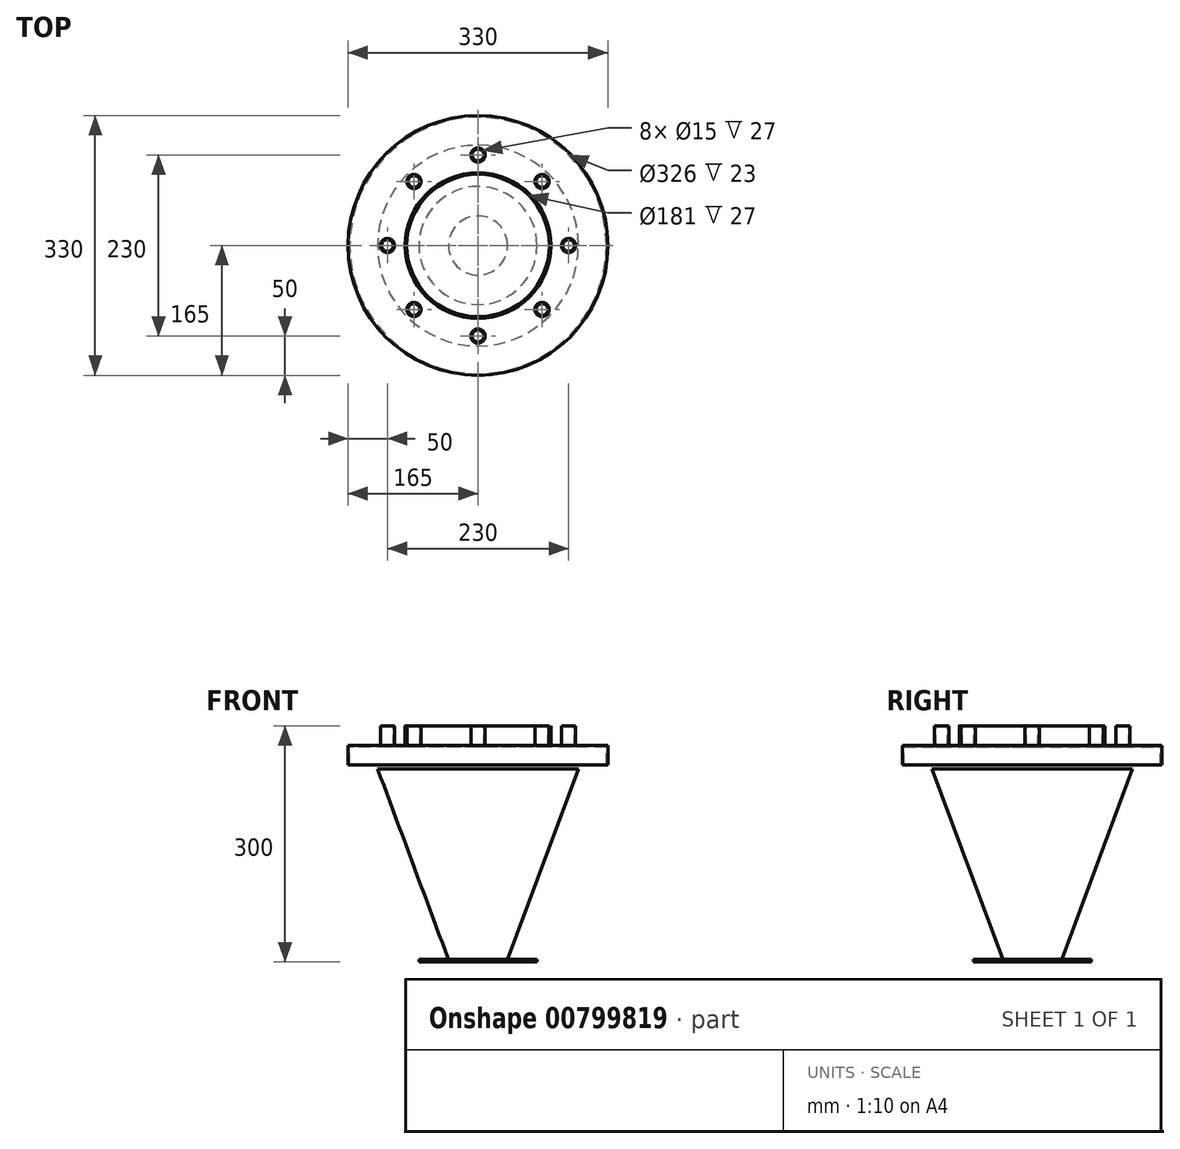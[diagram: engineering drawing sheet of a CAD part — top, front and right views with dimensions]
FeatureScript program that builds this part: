
annotation { "Feature Type Name" : "Feature", "Feature Type Description" : "" }
export const myFeature = defineFeature(function(context is Context, id is Id, definition is map)
    precondition{}
    {
        {
            var Q0;
            Q0=qCreatedBy(makeId("Front.planeOp"),FACE);
            var sketch = newSketch(context, id + "F0", { "sketchPlane" : qUnion([Q0])});
            skLineSegment(sketch, "E0", {"start": v(0, 0) * mm, "end": v(-127.5, 0) * mm});
            skLineSegment(sketch, "E1", {"start": v(-127.5, 0) * mm, "end": v(-37.5, -242) * mm});
            skLineSegment(sketch, "E2", {"start": v(-37.5, -242) * mm, "end": v(-75, -242) * mm});
            skLineSegment(sketch, "E3", {"start": v(-75, -242) * mm, "end": v(-75, -245) * mm});
            skLineSegment(sketch, "E4", {"start": v(-75, -245) * mm, "end": v(0, -245) * mm});
            skLineSegment(sketch, "E5", {"start": v(0, -245) * mm, "end": v(0, 0) * mm});
            skSolve(sketch);
        }
        {
            var Q0;
            Q0=makeQuery(id+"F0.imprint","IMPRINT",FACE,{"disambiguationData":[TD([[makeQuery(id+"F0.imprint","IMPRINT",EDGE,{"derivedFrom":sQuery(id+"F0.wireOp",EDGE,"E0")}),1.0]])]});
            var Q1;
            Q1=sQuery(id+"F0.wireOp",EDGE,"E5");
            revolve(context, id + "F1", {"surfaceOperationType" : NewSurfaceOperationType.NEW, "entities" : qUnion([Q0]), "axis" : qUnion([Q1]), "revolveType" : RevolveType.FULL});
        }
        {
            var Q0;
            Q0=qCreatedBy(makeId("Top.planeOp"),FACE);
            cPlane(context, id + "F2", {"entities" : qUnion([Q0]), "cplaneType" : CPlaneType.OFFSET, "offset" : 30 * mm, "width" : 150 * mm, "height" : 150 * mm});
        }
        {
            var Q0;
            Q0=qCreatedBy(id+"F2.planeOp",FACE);
            var sketch = newSketch(context, id + "F3", { "sketchPlane" : qUnion([Q0])});
            skCircle(sketch, "E6", {"center": v(0, 0) * mm, "radius": 165 * mm});
            skSolve(sketch);
        }
        {
            var Q0;
            Q0=makeQuery(id+"F3.imprint","IMPRINT",FACE,{"disambiguationData":[TD([[makeQuery(id+"F3.imprint","IMPRINT",EDGE,{"derivedFrom":sQuery(id+"F3.wireOp",EDGE,"E6")}),1.0]])]});
            extrude(context, id + "F4", {"entities" : qUnion([Q0]), "oppositeDirection" : true, "depth" : 25 * mm, "offsetDistance" : 25 * mm});
        }
        {
            var Q0;
            Q0=makeQuery(id+"F4.opExtrude","CAP_FACE",FACE,{"disambiguationData":[OSD([sQuery(id+"F3.wireOp",EDGE,"E6")])],"isStart":false});
            shell(context, id + "F5", {"entities" : qUnion([Q0]), "thickness" : 2 * mm});
        }
        {
            var Q0;
            Q0=qCreatedBy(id+"F2.planeOp",FACE);
            var sketch = newSketch(context, id + "F6", { "sketchPlane" : qUnion([Q0])});
            skCircle(sketch, "E7", {"center": v(0, 0) * mm, "radius": 92.5 * mm});
            skSolve(sketch);
        }
        {
            var Q0;
            Q0 = qSketchRegion(id + "F6", true);
            extrude(context, id + "F7", {"entities" : qUnion([Q0]), "operationType" : NewBodyOperationType.ADD, "depth" : 25 * mm, "offsetDistance" : 25 * mm});
        }
        {
            var Q0;
            Q0=makeQuery(id+"F7.opExtrude","CAP_FACE",FACE,{"disambiguationData":[OSD([sQuery(id+"F6.wireOp",EDGE,"E7")])],"isStart":false});
            shell(context, id + "F8", {"entities" : qUnion([Q0]), "thickness" : 2 * mm});
        }
        {
            var Q0;
            Q0=makeQuery(id+"F4.opExtrude","CAP_FACE",FACE,{"disambiguationData":[OSD([sQuery(id+"F3.wireOp",EDGE,"E6")])],"isStart":true});
            var sketch = newSketch(context, id + "F9", { "sketchPlane" : qUnion([Q0])});
            skCircle(sketch, "E8", {"center": v(0, 0) * mm, "radius": 90.5 * mm});
            skSolve(sketch);
        }
        {
            var Q0;
            Q0 = qSketchRegion(id + "F9", true);
            extrude(context, id + "F10", {"entities" : qUnion([Q0]), "operationType" : NewBodyOperationType.REMOVE, "oppositeDirection" : true, "depth" : 17 * mm, "offsetDistance" : 25 * mm});
        }
        {
            var Q0;
            Q0=makeQuery(id+"F4.opExtrude","CAP_FACE",FACE,{"disambiguationData":[OSD([sQuery(id+"F3.wireOp",EDGE,"E6")])],"isStart":true});
            var sketch = newSketch(context, id + "F11", { "sketchPlane" : qUnion([Q0])});
            skCircle(sketch, "E9", {"center": v(0, 115) * mm, "radius": 7.5 * mm});
            skCircle(sketch, "E10.1.0", {"center": v(-81.32, 81.32) * mm, "radius": 7.5 * mm});
            skCircle(sketch, "E10.2.0", {"center": v(-115, 0) * mm, "radius": 7.5 * mm});
            skCircle(sketch, "E10.3.0", {"center": v(-81.32, -81.32) * mm, "radius": 7.5 * mm});
            skCircle(sketch, "E10.4.0", {"center": v(0, -115) * mm, "radius": 7.5 * mm});
            skCircle(sketch, "E10.5.0", {"center": v(81.32, -81.32) * mm, "radius": 7.5 * mm});
            skCircle(sketch, "E10.6.0", {"center": v(115, 0) * mm, "radius": 7.5 * mm});
            skCircle(sketch, "E10.7.0", {"center": v(81.32, 81.32) * mm, "radius": 7.5 * mm});
            skPoint(sketch, "E10.center", {"position": v(0, 0) * mm});
            skSolve(sketch);
        }
        {
            var Q0;
            Q0 = qSketchRegion(id + "F11", true);
            extrude(context, id + "F12", {"entities" : qUnion([Q0]), "operationType" : NewBodyOperationType.REMOVE, "oppositeDirection" : true, "depth" : 25 * mm, "offsetDistance" : 25 * mm});
        }
        {
            var Q0;
            Q0=makeQuery(id+"F4.opExtrude","CAP_FACE",FACE,{"disambiguationData":[OSD([sQuery(id+"F3.wireOp",EDGE,"E6")])],"isStart":true});
            var sketch = newSketch(context, id + "F13", { "sketchPlane" : qUnion([Q0])});
            skCircle(sketch, "E11", {"center": v(0, 115) * mm, "radius": 7.5 * mm});
            skCircle(sketch, "E12", {"center": v(0, 115) * mm, "radius": 9 * mm});
            skCircle(sketch, "E13.3.0", {"center": v(0, -115) * mm, "radius": 9 * mm});
            skPoint(sketch, "E13.center", {"position": v(0, 0) * mm});
            skCircle(sketch, "E14.1.0", {"center": v(-81.32, 81.32) * mm, "radius": 7.5 * mm});
            skCircle(sketch, "E14.1.1", {"center": v(-81.32, 81.32) * mm, "radius": 9 * mm});
            skCircle(sketch, "E14.2.0", {"center": v(-115, 0) * mm, "radius": 7.5 * mm});
            skCircle(sketch, "E14.2.1", {"center": v(-115, 0) * mm, "radius": 9 * mm});
            skCircle(sketch, "E14.3.0", {"center": v(-81.32, -81.32) * mm, "radius": 7.5 * mm});
            skCircle(sketch, "E14.3.1", {"center": v(-81.32, -81.32) * mm, "radius": 9 * mm});
            skCircle(sketch, "E14.4.0", {"center": v(0, -115) * mm, "radius": 7.5 * mm});
            skCircle(sketch, "E14.5.0", {"center": v(81.32, -81.32) * mm, "radius": 7.5 * mm});
            skCircle(sketch, "E14.5.1", {"center": v(81.32, -81.32) * mm, "radius": 9 * mm});
            skCircle(sketch, "E14.6.0", {"center": v(115, 0) * mm, "radius": 7.5 * mm});
            skCircle(sketch, "E14.6.1", {"center": v(115, 0) * mm, "radius": 9 * mm});
            skCircle(sketch, "E14.7.0", {"center": v(81.32, 81.32) * mm, "radius": 7.5 * mm});
            skCircle(sketch, "E14.7.1", {"center": v(81.32, 81.32) * mm, "radius": 9 * mm});
            skSolve(sketch);
        }
        {
            var Q0;
            Q0 = qSketchRegion(id + "F13", true);
            extrude(context, id + "F14", {"entities" : qUnion([Q0]), "operationType" : NewBodyOperationType.ADD, "depth" : 25 * mm, "offsetDistance" : 25 * mm});
        }
    });
